# Revit family: Intono 1.1
name_source: partatom
category: Lighting Fixtures
revit_build: Autodesk Revit 2017 (Build: 20170419_0315(x64)
units: mm (PartAtom-declared; Revit-internal decimal feet)

## family parameters
Cut with Voids When Loaded = Yes
Host = Face
Light Source = Yes
Part Type = Normal
Room Calculation Point = Yes
Round Connector Dimension = Use Diameter
Shared = No

## types (3) — shared parameters
Apparent Load = 0 VA
Apparent Load Phase 1 = 3 W
Body = L&L_Die-cast aluminium
CRI = 90 (also available: CRI 80 - ref. URL Technical sheet)
Code = -
Color Filter = 16777215
Control system = -
Cutout dimensions = -
Default Elevation = 1219 mm
Delivered lumen output = 146 lm (3000K, 22°, CRI 80), 128 lm (3000K, 22°, CRI 90)
Description = Wall mounted for outdoor applications
Dimming Lamp Color Temperature Shift = <None>
Emit from Line Length = 610 mm
Energy efficiency class = A A+ A++
Features = -
Height mm = 90 mm  [stored 0.295276 ft]
IP = IP65
LED Colour = 3000K (also available: 2700K and 4000K - ref. URL Technical sheet)
Length mm = 30 mm  [stored 0.0984252 ft]
Lens = L&L_Tempered extra-clear glass
Lumen output at source = 168 lm (3000K, CRI 80), 147 lm (3000K, CRI 90)
Manufacturer = L&L Luce&Light
Material = body in die-cast aluminium, screen in black-serigraphed, tempered, transparent extra-clear glass
Model = Intono 1.1
Mounting = surface mounted (wall)
No. and type of led = 1 power LED, 1/4 ANSI BIN, 50 000h L90 B10 (Ta 25°C)
Notes = version compatible with Google Home or Amazon Echo available on request for voice command control
Power = 3W
Power cables = -
Power supply = 24Vdc
Power supply unit = not included
Screen = L&L_Black-serigraphed
Tilt Angle = 180.00°
Tiltable = -
URL = https://www.lucelight.it
URL Accessories and power supply units = https://www.lucelight.it
URL Catalogue = https://www.lucelight.it
URL DXF = https://www.lucelight.it
URL Description = https://www.lucelight.it
URL General code = https://www.lucelight.it
URL IES Photometric file = https://www.lucelight.it
URL Image = https://www.lucelight.it
URL Technical sheet = https://www.lucelight.it
Voltage = 24 V
Weight kg = 0.17 kg
Width mm = 46 mm  [stored 0.150919 ft]
Wiring = parallel

## per-type parameters (varying)
| type | Optics | Photometric Web File |
| Intono 1.1 L 33° (3000K 3W 24Vdc) | 33° | INTONO 1.1 L 33° [3000K 3W 24Vdc].IES |
| Intono 1.1 M 22° (3000K 3W 24Vdc) | 22° | INTONO 1.1 M 22° [3000K 3W 24Vdc].IES |
| Intono 1.1 S 13° (3000K 3W 24Vdc) | 13° | INTONO 1.1 S 13° [3000K 3W 24Vdc].IES |

note: [stored X ft] marks values corroborated as IEEE doubles in the binary element streams (Revit-internal decimal feet)

## geometry (parser evidence)
native form markers: Blend x2, Sweep x2
no freeform markers — native parametric forms only
